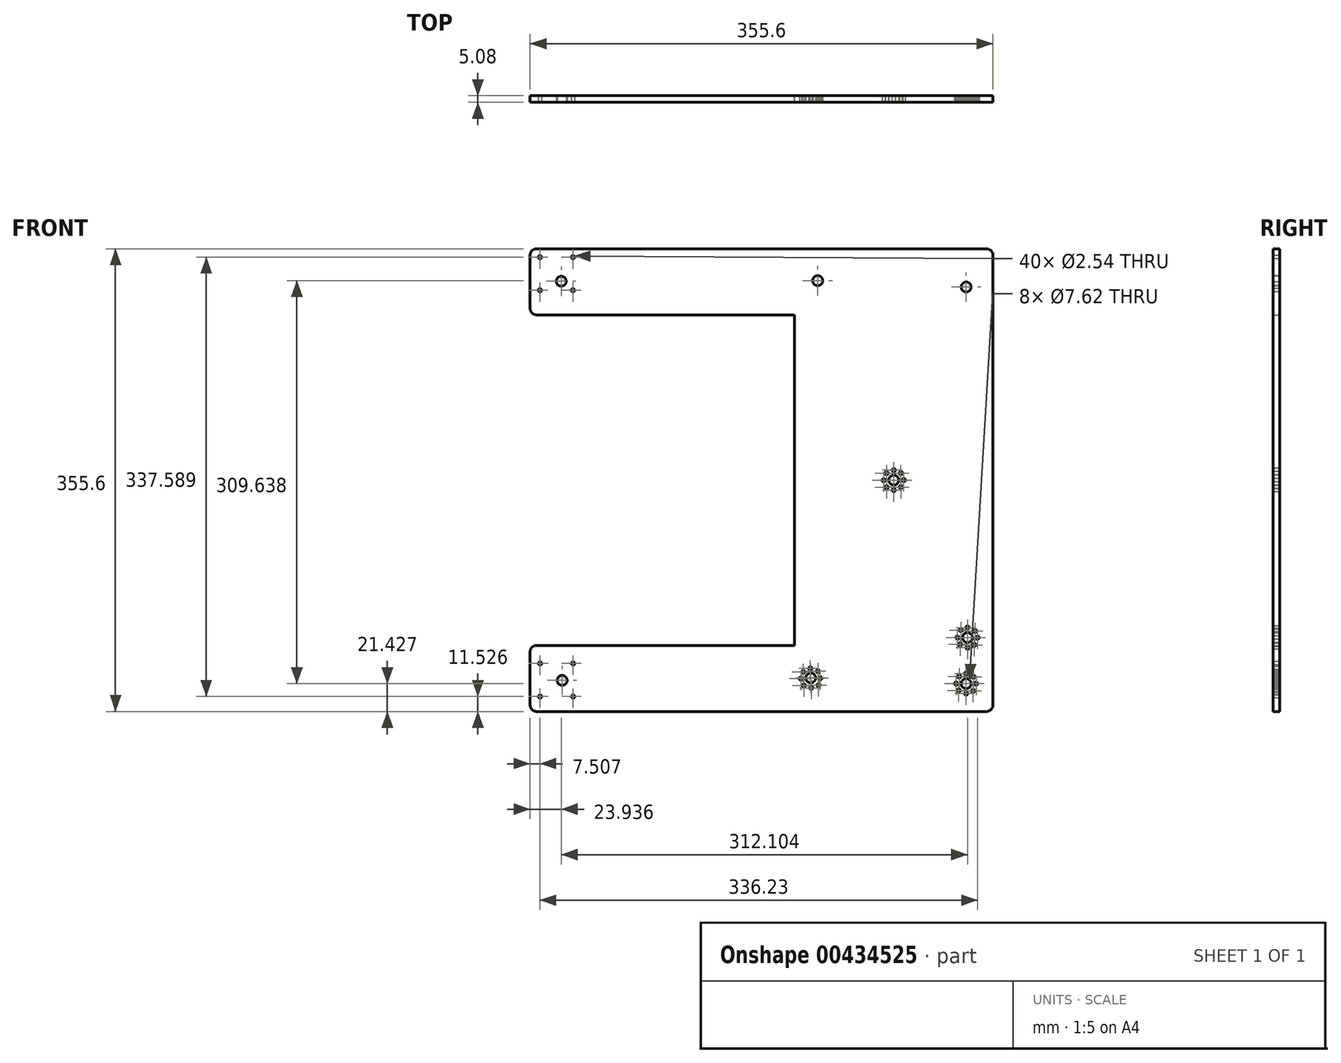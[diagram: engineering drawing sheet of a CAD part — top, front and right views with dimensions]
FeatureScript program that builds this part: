
annotation { "Feature Type Name" : "Feature", "Feature Type Description" : "" }
export const myFeature = defineFeature(function(context is Context, id is Id, definition is map)
    precondition{}
    {
        {
            var Q0;
            Q0=qCreatedBy(makeId("Front.planeOp"),FACE);
            var sketch = newSketch(context, id + "F0", { "sketchPlane" : qUnion([Q0])});
            skLineSegment(sketch, "E0.bottom", {"start": v(-177.8, 177.8) * mm, "end": v(27.5, 177.8) * mm});
            skLineSegment(sketch, "E0.left", {"start": v(-177.8, 177.8) * mm, "end": v(-177.8, 127) * mm});
            skLineSegment(sketch, "E0.right", {"start": v(177.8, 177.8) * mm, "end": v(177.8, -177.8) * mm});
            skPoint(sketch, "E0.middle", {"position": v(0, 0) * mm});
            skLineSegment(sketch, "E1", {"start": v(25.4, -177.8) * mm, "end": v(177.8, -177.8) * mm});
            skLineSegment(sketch, "E2", {"start": v(-177.8, 127) * mm, "end": v(25.4, 127) * mm});
            skLineSegment(sketch, "E3", {"start": v(25.4, 127) * mm, "end": v(25.4, -127) * mm});
            skLineSegment(sketch, "E4", {"start": v(25.4, -127) * mm, "end": v(-177.8, -127) * mm});
            skLineSegment(sketch, "E5.trimOffspring", {"start": v(-177.8, -127) * mm, "end": v(-177.8, -177.8) * mm});
            skLineSegment(sketch, "E6", {"start": v(27.5, 177.8) * mm, "end": v(177.8, 177.8) * mm});
            skLineSegment(sketch, "E7", {"start": v(-177.8, -177.8) * mm, "end": v(25.4, -177.8) * mm});
            skLineSegment(sketch, "E8", {"start": v(103.3, 0) * mm, "end": v(103.45, 0) * mm});
            skLineSegment(sketch, "E9.trimOffspring", {"start": v(97.1, -63.5) * mm, "end": v(97.1, -63.5) * mm});
            skSolve(sketch);
        }
        {
            var Q0;
            Q0=makeQuery(id+"F0.imprint","IMPRINT",FACE,{"disambiguationData":[TD([[makeQuery(id+"F0.imprint","IMPRINT",EDGE,{"derivedFrom":sQuery(id+"F0.wireOp",EDGE,"E0.bottom")}),-1.0]])]});
            extrude(context, id + "F1", {"entities" : qUnion([Q0]), "depth" : 5.08 * mm, "offsetDistance" : 25.4 * mm});
        }
        {
            var Q0;
            Q0=makeQuery(id+"F1.opExtrude","CAP_FACE",FACE,{"disambiguationData":[OSD([sQuery(id+"F0.wireOp",EDGE,"E0.bottom"),sQuery(id+"F0.wireOp",EDGE,"E0.left"),sQuery(id+"F0.wireOp",EDGE,"E0.right"),sQuery(id+"F0.wireOp",EDGE,"E1"),sQuery(id+"F0.wireOp",EDGE,"E2"),sQuery(id+"F0.wireOp",EDGE,"E3"),sQuery(id+"F0.wireOp",EDGE,"E4"),sQuery(id+"F0.wireOp",EDGE,"E5.trimOffspring"),sQuery(id+"F0.wireOp",EDGE,"E6"),sQuery(id+"F0.wireOp",EDGE,"E7")])],"isStart":false});
            var sketch = newSketch(context, id + "F2", { "sketchPlane" : qUnion([Q0])});
            skCircle(sketch, "E10", {"center": v(-153.86, 152.82) * mm, "radius": 3.81 * mm});
            skCircle(sketch, "E11", {"center": v(101.6, 0) * mm, "radius": 3.81 * mm});
            skPoint(sketch, "E12", {"position": v(177.8, 0) * mm});
            skPoint(sketch, "E13.orphan", {"position": v(25.4, 0) * mm});
            skCircle(sketch, "E14", {"center": v(-153.16, -153.89) * mm, "radius": 3.81 * mm});
            skCircle(sketch, "E15", {"center": v(157.18, -156.37) * mm, "radius": 3.81 * mm});
            skLineSegment(sketch, "E16", {"start": v(-153.86, 152.82) * mm, "end": v(-150.05, 152.82) * mm});
            skLineSegment(sketch, "E17", {"start": v(157.18, 148.43) * mm, "end": v(157.18, -156.37) * mm});
            skCircle(sketch, "E18", {"center": v(157.18, 148.43) * mm, "radius": 3.81 * mm});
            skSolve(sketch);
        }
        {
            var Q0;
            Q0=sQuery(id+"F2.wireOp",VERTEX,"E10.center");
            var Q1;
            Q1=sQuery(id+"F2.wireOp",VERTEX,"E11.center");
            var Q2;
            Q2=sQuery(id+"F2.wireOp",VERTEX,"E14.center");
            var Q3;
            Q3=sQuery(id+"F2.wireOp",VERTEX,"sf762GB6-AUzR-9Akw-79fv-GTK4VFTHom6u.center");
            var Q4;
            Q4=sQuery(id+"F2.wireOp",VERTEX,"E15.center");
            var Q5;
            Q5=sQuery(id+"F2.wireOp",VERTEX,"E17.start");
            var Q6;
            Q6=makeQuery(id+"F1.opExtrude","SWEPT_BODY",BODY,{"disambiguationData":[OSD([sQuery(id+"F0.wireOp",EDGE,"E0.bottom"),sQuery(id+"F0.wireOp",EDGE,"E0.left"),sQuery(id+"F0.wireOp",EDGE,"E0.right"),sQuery(id+"F0.wireOp",EDGE,"E1"),sQuery(id+"F0.wireOp",EDGE,"E2"),sQuery(id+"F0.wireOp",EDGE,"E3"),sQuery(id+"F0.wireOp",EDGE,"E4"),sQuery(id+"F0.wireOp",EDGE,"E5.trimOffspring"),sQuery(id+"F0.wireOp",EDGE,"E6"),sQuery(id+"F0.wireOp",EDGE,"E7")])]});
            hole(context, id + "F3", {"style" : HoleStyle.SIMPLE, "endStyle" : HoleEndStyle.THROUGH, "holeDiameter" : 7.62 * mm, "isTappedThrough" : true, "tappedDepth" : 12.7 * mm, "tapClearance" : 3, "locations" : qUnion([Q0, Q1, Q2, Q3, Q4, Q5]), "scope" : qUnion([Q6])});
        }
        {
            var Q0;
            Q0=makeQuery(id+"F1.opExtrude","SWEPT_EDGE",EDGE,{"disambiguationData":[OSD([sQuery(id+"F0.wireOp",EDGE,"E0.right"),sQuery(id+"F0.wireOp",EDGE,"E6")])]});
            var Q1;
            Q1=makeQuery(id+"F1.opExtrude","SWEPT_EDGE",EDGE,{"disambiguationData":[OSD([sQuery(id+"F0.wireOp",EDGE,"E0.bottom"),sQuery(id+"F0.wireOp",EDGE,"E0.left")])]});
            var Q2;
            Q2=makeQuery(id+"F1.opExtrude","SWEPT_EDGE",EDGE,{"disambiguationData":[OSD([sQuery(id+"F0.wireOp",EDGE,"E0.left"),sQuery(id+"F0.wireOp",EDGE,"E2")])]});
            var Q3;
            Q3=makeQuery(id+"F1.opExtrude","SWEPT_EDGE",EDGE,{"disambiguationData":[OSD([sQuery(id+"F0.wireOp",EDGE,"E4"),sQuery(id+"F0.wireOp",EDGE,"E5.trimOffspring")])]});
            var Q4;
            Q4=makeQuery(id+"F1.opExtrude","SWEPT_EDGE",EDGE,{"disambiguationData":[OSD([sQuery(id+"F0.wireOp",EDGE,"E5.trimOffspring"),sQuery(id+"F0.wireOp",EDGE,"E7")])]});
            var Q5;
            Q5=makeQuery(id+"F1.opExtrude","SWEPT_EDGE",EDGE,{"disambiguationData":[OSD([sQuery(id+"F0.wireOp",EDGE,"E0.right"),sQuery(id+"F0.wireOp",EDGE,"E1")])]});
            fillet(context, id + "F4", {"entities" : qUnion([Q0, Q1, Q2, Q3, Q4, Q5]), "radius" : 5.08 * mm, "tangentPropagation" : true, "allowEdgeOverflow" : false});
        }
        {
            var Q0;
            Q0=makeQuery(id+"F1.opExtrude","CAP_FACE",FACE,{"disambiguationData":[OSD([sQuery(id+"F0.wireOp",EDGE,"E0.bottom"),sQuery(id+"F0.wireOp",EDGE,"E0.left"),sQuery(id+"F0.wireOp",EDGE,"E0.right"),sQuery(id+"F0.wireOp",EDGE,"E1"),sQuery(id+"F0.wireOp",EDGE,"E2"),sQuery(id+"F0.wireOp",EDGE,"E3"),sQuery(id+"F0.wireOp",EDGE,"E4"),sQuery(id+"F0.wireOp",EDGE,"E5.trimOffspring"),sQuery(id+"F0.wireOp",EDGE,"E6"),sQuery(id+"F0.wireOp",EDGE,"E7")])],"isStart":false});
            var sketch = newSketch(context, id + "F5", { "sketchPlane" : qUnion([Q0])});
            skCircle(sketch, "E19", {"center": v(101.6, 7.7) * mm, "radius": 1.27 * mm});
            skCircle(sketch, "E20", {"center": v(109.3, 0) * mm, "radius": 1.27 * mm});
            skCircle(sketch, "E21", {"center": v(101.6, -7.7) * mm, "radius": 1.27 * mm});
            skCircle(sketch, "E22", {"center": v(93.9, 0) * mm, "radius": 1.27 * mm});
            skCircle(sketch, "E23", {"center": v(-144.9, 171.31) * mm, "radius": 2.54 * mm});
            skCircle(sketch, "E24", {"center": v(-144.9, 145.91) * mm, "radius": 2.54 * mm});
            skCircle(sketch, "E25", {"center": v(-170.3, 145.91) * mm, "radius": 2.54 * mm});
            skCircle(sketch, "E26", {"center": v(-170.3, 171.31) * mm, "radius": 2.54 * mm});
            skCircle(sketch, "E27", {"center": v(157.18, -148.68) * mm, "radius": 1.27 * mm});
            skCircle(sketch, "E28", {"center": v(151.85, -150.82) * mm, "radius": 1.27 * mm});
            skCircle(sketch, "E29", {"center": v(157.18, -164.07) * mm, "radius": 1.27 * mm});
            skCircle(sketch, "E30", {"center": v(162.5, -161.94) * mm, "radius": 1.27 * mm});
            skCircle(sketch, "E31", {"center": v(-170.16, -140.87) * mm, "radius": 2.54 * mm});
            skCircle(sketch, "E32", {"center": v(-144.76, -140.87) * mm, "radius": 2.54 * mm});
            skCircle(sketch, "E33", {"center": v(-144.76, -166.27) * mm, "radius": 2.54 * mm});
            skCircle(sketch, "E34", {"center": v(-170.16, -166.27) * mm, "radius": 2.54 * mm});
            skPoint(sketch, "E35.start.orphan", {"position": v(101.6, 0) * mm});
            skCircle(sketch, "E36", {"center": v(107.05, 5.43) * mm, "radius": 1.27 * mm});
            skCircle(sketch, "E37", {"center": v(96.09, 5.37) * mm, "radius": 1.27 * mm});
            skCircle(sketch, "E38", {"center": v(96.17, -5.45) * mm, "radius": 1.27 * mm});
            skCircle(sketch, "E39", {"center": v(107.12, -5.37) * mm, "radius": 1.27 * mm});
            skPoint(sketch, "E40.orphan", {"position": v(157.18, 148.43) * mm});
            skCircle(sketch, "E41", {"center": v(149.48, -156.37) * mm, "radius": 1.27 * mm});
            skCircle(sketch, "E42", {"center": v(162.79, -151.1) * mm, "radius": 1.27 * mm});
            skCircle(sketch, "E43", {"center": v(164.87, -156.37) * mm, "radius": 1.27 * mm});
            skCircle(sketch, "E44", {"center": v(151.53, -161.6) * mm, "radius": 1.27 * mm});
            skLineSegment(sketch, "E45", {"start": v(101.6, 0) * mm, "end": v(109.3, 0) * mm});
            skSolve(sketch);
        }
        {
            var Q0;
            Q0=sQuery(id+"F5.wireOp",VERTEX,"E22.center");
            var Q1;
            Q1=sQuery(id+"F5.wireOp",VERTEX,"E19.center");
            var Q2;
            Q2=sQuery(id+"F5.wireOp",VERTEX,"E20.center");
            var Q3;
            Q3=sQuery(id+"F5.wireOp",VERTEX,"E21.center");
            var Q4;
            Q4=sQuery(id+"F5.wireOp",VERTEX,"E31.center");
            var Q5;
            Q5=sQuery(id+"F5.wireOp",VERTEX,"E32.center");
            var Q6;
            Q6=sQuery(id+"F5.wireOp",VERTEX,"E34.center");
            var Q7;
            Q7=sQuery(id+"F5.wireOp",VERTEX,"E33.center");
            var Q8;
            Q8=sQuery(id+"F5.wireOp",VERTEX,"E27.center");
            var Q9;
            Q9=sQuery(id+"F5.wireOp",VERTEX,"E28.center");
            var Q10;
            Q10=sQuery(id+"F5.wireOp",VERTEX,"E30.center");
            var Q11;
            Q11=sQuery(id+"F5.wireOp",VERTEX,"E29.center");
            var Q12;
            Q12=sQuery(id+"F5.wireOp",VERTEX,"7gKi7Xx8-Owrd-ScP1-hQiL-wp9ljm8E0cgy.center");
            var Q13;
            Q13=sQuery(id+"F5.wireOp",VERTEX,"U4azVyad-7BIC-DalR-FYGB-97zGRGCuIKDm.center");
            var Q14;
            Q14=sQuery(id+"F5.wireOp",VERTEX,"w9TwhmPk-EQ9W-INRI-itxZ-VNiDpz6awa4o.center");
            var Q15;
            Q15=sQuery(id+"F5.wireOp",VERTEX,"WGOVrJEy-sgWF-f4I0-O2PT-7mHf3WImSYyX.center");
            var Q16;
            Q16=sQuery(id+"F5.wireOp",VERTEX,"E26.center");
            var Q17;
            Q17=sQuery(id+"F5.wireOp",VERTEX,"E23.center");
            var Q18;
            Q18=sQuery(id+"F5.wireOp",VERTEX,"E24.center");
            var Q19;
            Q19=sQuery(id+"F5.wireOp",VERTEX,"E25.center");
            var Q20;
            Q20=sQuery(id+"F5.wireOp",VERTEX,"E37.center");
            var Q21;
            Q21=sQuery(id+"F5.wireOp",VERTEX,"E36.center");
            var Q22;
            Q22=sQuery(id+"F5.wireOp",VERTEX,"E39.center");
            var Q23;
            Q23=sQuery(id+"F5.wireOp",VERTEX,"E38.center");
            var Q24;
            Q24=sQuery(id+"F5.wireOp",VERTEX,"E41.center");
            var Q25;
            Q25=sQuery(id+"F5.wireOp",VERTEX,"E44.center");
            var Q26;
            Q26=sQuery(id+"F5.wireOp",VERTEX,"E43.center");
            var Q27;
            Q27=sQuery(id+"F5.wireOp",VERTEX,"E42.center");
            var Q28;
            Q28=makeQuery(id+"F1.opExtrude","SWEPT_BODY",BODY,{"disambiguationData":[OSD([sQuery(id+"F0.wireOp",EDGE,"E0.bottom"),sQuery(id+"F0.wireOp",EDGE,"E0.left"),sQuery(id+"F0.wireOp",EDGE,"E0.right"),sQuery(id+"F0.wireOp",EDGE,"E1"),sQuery(id+"F0.wireOp",EDGE,"E2"),sQuery(id+"F0.wireOp",EDGE,"E3"),sQuery(id+"F0.wireOp",EDGE,"E4"),sQuery(id+"F0.wireOp",EDGE,"E5.trimOffspring"),sQuery(id+"F0.wireOp",EDGE,"E6"),sQuery(id+"F0.wireOp",EDGE,"E7")])]});
            hole(context, id + "F6", {"style" : HoleStyle.SIMPLE, "endStyle" : HoleEndStyle.THROUGH, "holeDiameter" : 2.54 * mm, "tappedDepth" : 12.7 * mm, "tapClearance" : 3, "locations" : qUnion([Q0, Q1, Q2, Q3, Q4, Q5, Q6, Q7, Q8, Q9, Q10, Q11, Q12, Q13, Q14, Q15, Q16, Q17, Q18, Q19, Q20, Q21, Q22, Q23, Q24, Q25, Q26, Q27]), "scope" : qUnion([Q28])});
        }
        {
            var Q0;
            Q0=makeQuery(id+"F1.opExtrude","CAP_FACE",FACE,{"disambiguationData":[OSD([sQuery(id+"F0.wireOp",EDGE,"E0.bottom"),sQuery(id+"F0.wireOp",EDGE,"E0.left"),sQuery(id+"F0.wireOp",EDGE,"E0.right"),sQuery(id+"F0.wireOp",EDGE,"E1"),sQuery(id+"F0.wireOp",EDGE,"E2"),sQuery(id+"F0.wireOp",EDGE,"E3"),sQuery(id+"F0.wireOp",EDGE,"E4"),sQuery(id+"F0.wireOp",EDGE,"E5.trimOffspring"),sQuery(id+"F0.wireOp",EDGE,"E6"),sQuery(id+"F0.wireOp",EDGE,"E7")])],"isStart":true});
            var sketch = newSketch(context, id + "F7", { "sketchPlane" : qUnion([Q0])});
            skCircle(sketch, "E46", {"center": v(-158.24, -121.02) * mm, "radius": 3.81 * mm});
            skPoint(sketch, "E47.orphan", {"position": v(-157.18, 148.43) * mm});
            skSolve(sketch);
        }
        {
            var Q0;
            Q0=sQuery(id+"F7.wireOp",VERTEX,"E46.center");
            var Q1;
            Q1=makeQuery(id+"F1.opExtrude","SWEPT_BODY",BODY,{"disambiguationData":[OSD([sQuery(id+"F0.wireOp",EDGE,"E0.bottom"),sQuery(id+"F0.wireOp",EDGE,"E0.left"),sQuery(id+"F0.wireOp",EDGE,"E0.right"),sQuery(id+"F0.wireOp",EDGE,"E1"),sQuery(id+"F0.wireOp",EDGE,"E2"),sQuery(id+"F0.wireOp",EDGE,"E3"),sQuery(id+"F0.wireOp",EDGE,"E4"),sQuery(id+"F0.wireOp",EDGE,"E5.trimOffspring"),sQuery(id+"F0.wireOp",EDGE,"E6"),sQuery(id+"F0.wireOp",EDGE,"E7")])]});
            hole(context, id + "F8", {"style" : HoleStyle.SIMPLE, "endStyle" : HoleEndStyle.THROUGH, "holeDiameter" : 7.62 * mm, "tappedDepth" : 12.7 * mm, "tapClearance" : 3, "locations" : qUnion([Q0]), "scope" : qUnion([Q1])});
        }
        {
            var Q0;
            Q0=makeQuery(id+"F1.opExtrude","CAP_FACE",FACE,{"disambiguationData":[OSD([sQuery(id+"F0.wireOp",EDGE,"E0.bottom"),sQuery(id+"F0.wireOp",EDGE,"E0.left"),sQuery(id+"F0.wireOp",EDGE,"E0.right"),sQuery(id+"F0.wireOp",EDGE,"E1"),sQuery(id+"F0.wireOp",EDGE,"E2"),sQuery(id+"F0.wireOp",EDGE,"E3"),sQuery(id+"F0.wireOp",EDGE,"E4"),sQuery(id+"F0.wireOp",EDGE,"E5.trimOffspring"),sQuery(id+"F0.wireOp",EDGE,"E6"),sQuery(id+"F0.wireOp",EDGE,"E7")])],"isStart":false});
            var sketch = newSketch(context, id + "F9", { "sketchPlane" : qUnion([Q0])});
            skCircle(sketch, "E48", {"center": v(165.94, -121.02) * mm, "radius": 1.27 * mm});
            skCircle(sketch, "E49", {"center": v(158.24, -128.72) * mm, "radius": 1.27 * mm});
            skCircle(sketch, "E50", {"center": v(150.54, -121.02) * mm, "radius": 1.27 * mm});
            skCircle(sketch, "E51", {"center": v(158.24, -113.33) * mm, "radius": 1.27 * mm});
            skPoint(sketch, "E52.orphan", {"position": v(158.24, -121.02) * mm});
            skCircle(sketch, "E53", {"center": v(164, -115.92) * mm, "radius": 1.27 * mm});
            skCircle(sketch, "E54", {"center": v(163.5, -126.65) * mm, "radius": 1.27 * mm});
            skCircle(sketch, "E55", {"center": v(152.55, -126.2) * mm, "radius": 1.27 * mm});
            skCircle(sketch, "E56", {"center": v(153.2, -115.21) * mm, "radius": 1.27 * mm});
            skLineSegment(sketch, "E57", {"start": v(158.24, -121.02) * mm, "end": v(164, -115.92) * mm});
            skLineSegment(sketch, "E58", {"start": v(163.5, -126.65) * mm, "end": v(158.24, -121.02) * mm});
            skLineSegment(sketch, "E59", {"start": v(152.55, -126.2) * mm, "end": v(158.24, -121.02) * mm});
            skLineSegment(sketch, "E60", {"start": v(153.2, -115.21) * mm, "end": v(158.24, -121.02) * mm});
            skSolve(sketch);
        }
        {
            var Q0;
            Q0=sQuery(id+"F9.wireOp",VERTEX,"E48.center");
            var Q1;
            Q1=sQuery(id+"F9.wireOp",VERTEX,"E57.end");
            var Q2;
            Q2=sQuery(id+"F9.wireOp",VERTEX,"E58.start");
            var Q3;
            Q3=sQuery(id+"F9.wireOp",VERTEX,"E49.center");
            var Q4;
            Q4=sQuery(id+"F9.wireOp",VERTEX,"E59.start");
            var Q5;
            Q5=sQuery(id+"F9.wireOp",VERTEX,"E50.center");
            var Q6;
            Q6=sQuery(id+"F9.wireOp",VERTEX,"E60.start");
            var Q7;
            Q7=sQuery(id+"F9.wireOp",VERTEX,"E51.center");
            var Q8;
            Q8=makeQuery(id+"F1.opExtrude","SWEPT_BODY",BODY,{"disambiguationData":[OSD([sQuery(id+"F0.wireOp",EDGE,"E0.bottom"),sQuery(id+"F0.wireOp",EDGE,"E0.left"),sQuery(id+"F0.wireOp",EDGE,"E0.right"),sQuery(id+"F0.wireOp",EDGE,"E1"),sQuery(id+"F0.wireOp",EDGE,"E2"),sQuery(id+"F0.wireOp",EDGE,"E3"),sQuery(id+"F0.wireOp",EDGE,"E4"),sQuery(id+"F0.wireOp",EDGE,"E5.trimOffspring"),sQuery(id+"F0.wireOp",EDGE,"E6"),sQuery(id+"F0.wireOp",EDGE,"E7")])]});
            hole(context, id + "F10", {"style" : HoleStyle.SIMPLE, "endStyle" : HoleEndStyle.THROUGH, "holeDiameter" : 2.54 * mm, "tappedDepth" : 12.7 * mm, "tapClearance" : 3, "locations" : qUnion([Q0, Q1, Q2, Q3, Q4, Q5, Q6, Q7]), "scope" : qUnion([Q8])});
        }
        {
            var Q0;
            Q0=makeQuery(id+"F1.opExtrude","CAP_FACE",FACE,{"disambiguationData":[OSD([sQuery(id+"F0.wireOp",EDGE,"E0.bottom"),sQuery(id+"F0.wireOp",EDGE,"E0.left"),sQuery(id+"F0.wireOp",EDGE,"E0.right"),sQuery(id+"F0.wireOp",EDGE,"E1"),sQuery(id+"F0.wireOp",EDGE,"E2"),sQuery(id+"F0.wireOp",EDGE,"E3"),sQuery(id+"F0.wireOp",EDGE,"E4"),sQuery(id+"F0.wireOp",EDGE,"E5.trimOffspring"),sQuery(id+"F0.wireOp",EDGE,"E6"),sQuery(id+"F0.wireOp",EDGE,"E7")])],"isStart":false});
            var sketch = newSketch(context, id + "F11", { "sketchPlane" : qUnion([Q0])});
            skCircle(sketch, "E61", {"center": v(37.46, -144.67) * mm, "radius": 1.27 * mm});
            skCircle(sketch, "E62", {"center": v(30.28, -152.57) * mm, "radius": 1.27 * mm});
            skCircle(sketch, "E63", {"center": v(38.29, -159.7) * mm, "radius": 1.33 * mm});
            skCircle(sketch, "E64", {"center": v(45.08, -152.3) * mm, "radius": 1.27 * mm});
            skCircle(sketch, "E65", {"center": v(43.32, -146.81) * mm, "radius": 1.27 * mm});
            skCircle(sketch, "E66", {"center": v(43.9, -157.54) * mm, "radius": 1.27 * mm});
            skCircle(sketch, "E67", {"center": v(32.54, -157.83) * mm, "radius": 1.27 * mm});
            skCircle(sketch, "E68", {"center": v(32.06, -147.31) * mm, "radius": 1.27 * mm});
            skSolve(sketch);
        }
        {
            var Q0;
            Q0=sQuery(id+"F11.wireOp",VERTEX,"E68.center");
            var Q1;
            Q1=sQuery(id+"F11.wireOp",VERTEX,"E61.center");
            var Q2;
            Q2=sQuery(id+"F11.wireOp",VERTEX,"E65.center");
            var Q3;
            Q3=sQuery(id+"F11.wireOp",VERTEX,"E64.center");
            var Q4;
            Q4=sQuery(id+"F11.wireOp",VERTEX,"E66.center");
            var Q5;
            Q5=sQuery(id+"F11.wireOp",VERTEX,"E63.center");
            var Q6;
            Q6=sQuery(id+"F11.wireOp",VERTEX,"E67.center");
            var Q7;
            Q7=sQuery(id+"F11.wireOp",VERTEX,"E62.center");
            var Q8;
            Q8=makeQuery(id+"F1.opExtrude","SWEPT_BODY",BODY,{"disambiguationData":[OSD([sQuery(id+"F0.wireOp",EDGE,"E0.bottom"),sQuery(id+"F0.wireOp",EDGE,"E0.left"),sQuery(id+"F0.wireOp",EDGE,"E0.right"),sQuery(id+"F0.wireOp",EDGE,"E1"),sQuery(id+"F0.wireOp",EDGE,"E2"),sQuery(id+"F0.wireOp",EDGE,"E3"),sQuery(id+"F0.wireOp",EDGE,"E4"),sQuery(id+"F0.wireOp",EDGE,"E5.trimOffspring"),sQuery(id+"F0.wireOp",EDGE,"E6"),sQuery(id+"F0.wireOp",EDGE,"E7")])]});
            hole(context, id + "F12", {"style" : HoleStyle.SIMPLE, "endStyle" : HoleEndStyle.THROUGH, "holeDiameter" : 2.54 * mm, "tappedDepth" : 12.7 * mm, "tapClearance" : 3, "locations" : qUnion([Q0, Q1, Q2, Q3, Q4, Q5, Q6, Q7]), "scope" : qUnion([Q8])});
        }
        {
            var Q0;
            Q0=makeQuery(id+"F1.opExtrude","CAP_FACE",FACE,{"disambiguationData":[OSD([sQuery(id+"F0.wireOp",EDGE,"E0.bottom"),sQuery(id+"F0.wireOp",EDGE,"E0.left"),sQuery(id+"F0.wireOp",EDGE,"E0.right"),sQuery(id+"F0.wireOp",EDGE,"E1"),sQuery(id+"F0.wireOp",EDGE,"E2"),sQuery(id+"F0.wireOp",EDGE,"E3"),sQuery(id+"F0.wireOp",EDGE,"E4"),sQuery(id+"F0.wireOp",EDGE,"E5.trimOffspring"),sQuery(id+"F0.wireOp",EDGE,"E6"),sQuery(id+"F0.wireOp",EDGE,"E7")])],"isStart":false});
            var sketch = newSketch(context, id + "F13", { "sketchPlane" : qUnion([Q0])});
            skCircle(sketch, "E69", {"center": v(37.78, -151.95) * mm, "radius": 3.81 * mm});
            skSolve(sketch);
        }
        {
            var Q0;
            Q0=sQuery(id+"F13.wireOp",VERTEX,"E69.center");
            var Q1;
            Q1=makeQuery(id+"F1.opExtrude","SWEPT_BODY",BODY,{"disambiguationData":[OSD([sQuery(id+"F0.wireOp",EDGE,"E0.bottom"),sQuery(id+"F0.wireOp",EDGE,"E0.left"),sQuery(id+"F0.wireOp",EDGE,"E0.right"),sQuery(id+"F0.wireOp",EDGE,"E1"),sQuery(id+"F0.wireOp",EDGE,"E2"),sQuery(id+"F0.wireOp",EDGE,"E3"),sQuery(id+"F0.wireOp",EDGE,"E4"),sQuery(id+"F0.wireOp",EDGE,"E5.trimOffspring"),sQuery(id+"F0.wireOp",EDGE,"E6"),sQuery(id+"F0.wireOp",EDGE,"E7")])]});
            hole(context, id + "F14", {"style" : HoleStyle.SIMPLE, "endStyle" : HoleEndStyle.THROUGH, "holeDiameter" : 7.62 * mm, "tappedDepth" : 12.7 * mm, "tapClearance" : 3, "locations" : qUnion([Q0]), "scope" : qUnion([Q1])});
        }
        {
            var Q0;
            Q0=makeQuery(id+"F1.opExtrude","CAP_FACE",FACE,{"disambiguationData":[OSD([sQuery(id+"F0.wireOp",EDGE,"E0.bottom"),sQuery(id+"F0.wireOp",EDGE,"E0.left"),sQuery(id+"F0.wireOp",EDGE,"E0.right"),sQuery(id+"F0.wireOp",EDGE,"E1"),sQuery(id+"F0.wireOp",EDGE,"E2"),sQuery(id+"F0.wireOp",EDGE,"E3"),sQuery(id+"F0.wireOp",EDGE,"E4"),sQuery(id+"F0.wireOp",EDGE,"E5.trimOffspring"),sQuery(id+"F0.wireOp",EDGE,"E6"),sQuery(id+"F0.wireOp",EDGE,"E7")])],"isStart":false});
            var sketch = newSketch(context, id + "F15", { "sketchPlane" : qUnion([Q0])});
            skCircle(sketch, "E70", {"center": v(43.13, 153.26) * mm, "radius": 3.81 * mm});
            skSolve(sketch);
        }
        {
            var Q0;
            Q0=sQuery(id+"F15.wireOp",VERTEX,"E70.center");
            var Q1;
            Q1=makeQuery(id+"F1.opExtrude","SWEPT_BODY",BODY,{"disambiguationData":[OSD([sQuery(id+"F0.wireOp",EDGE,"E0.bottom"),sQuery(id+"F0.wireOp",EDGE,"E0.left"),sQuery(id+"F0.wireOp",EDGE,"E0.right"),sQuery(id+"F0.wireOp",EDGE,"E1"),sQuery(id+"F0.wireOp",EDGE,"E2"),sQuery(id+"F0.wireOp",EDGE,"E3"),sQuery(id+"F0.wireOp",EDGE,"E4"),sQuery(id+"F0.wireOp",EDGE,"E5.trimOffspring"),sQuery(id+"F0.wireOp",EDGE,"E6"),sQuery(id+"F0.wireOp",EDGE,"E7")])]});
            hole(context, id + "F16", {"style" : HoleStyle.SIMPLE, "endStyle" : HoleEndStyle.THROUGH, "holeDiameter" : 7.62 * mm, "isTappedThrough" : true, "tappedDepth" : 12.7 * mm, "tapClearance" : 3, "locations" : qUnion([Q0]), "scope" : qUnion([Q1])});
        }
    });
